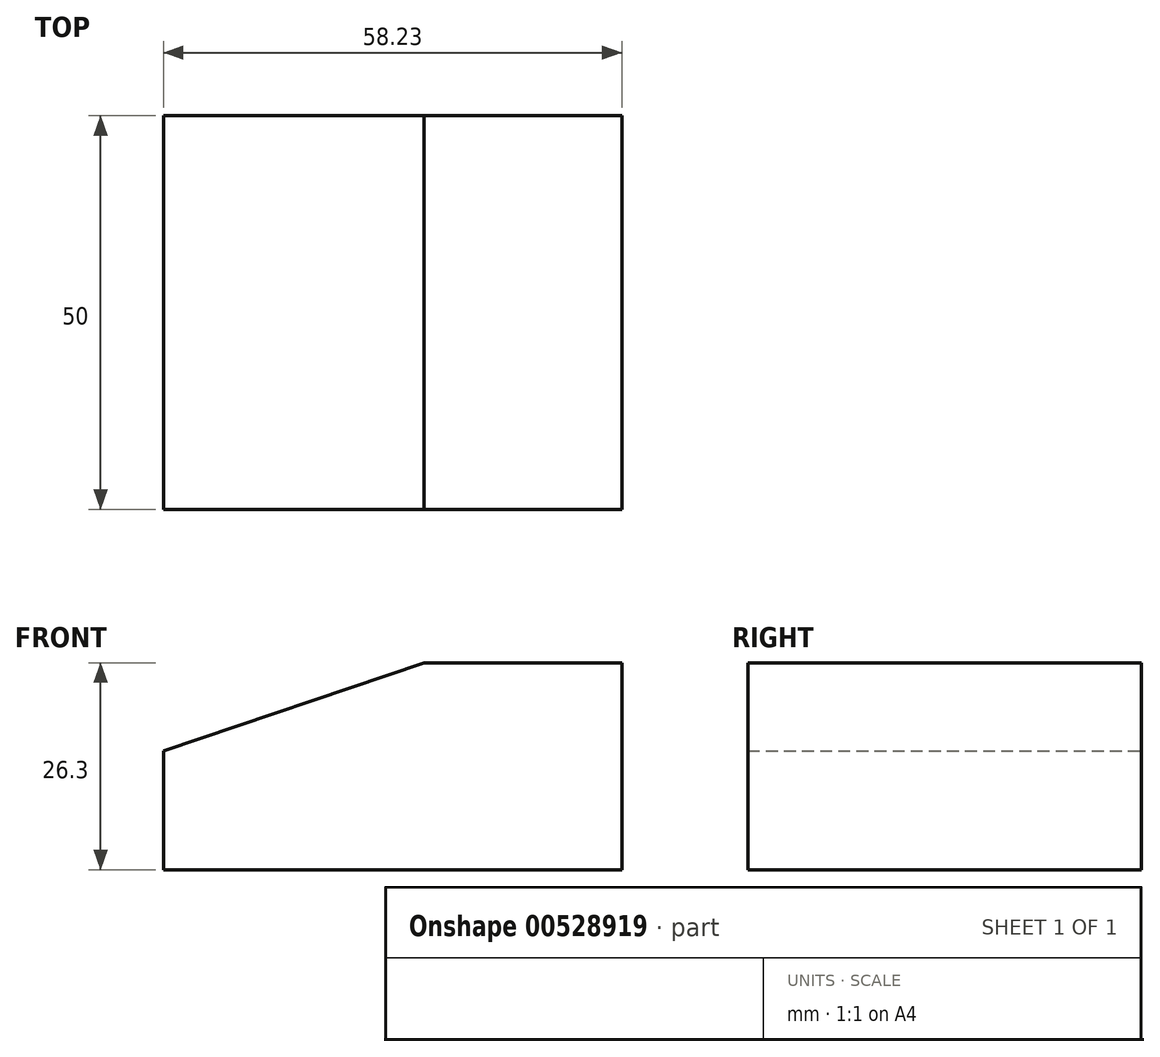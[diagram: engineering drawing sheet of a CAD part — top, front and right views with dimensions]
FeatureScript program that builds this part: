
annotation { "Feature Type Name" : "Feature", "Feature Type Description" : "" }
export const myFeature = defineFeature(function(context is Context, id is Id, definition is map)
    precondition{}
    {
        {
            var Q0;
            Q0=qCreatedBy(makeId("Front.planeOp"),FACE);
            var sketch = newSketch(context, id + "F0", { "sketchPlane" : qUnion([Q0])});
            skLineSegment(sketch, "E0", {"start": v(-58.23, 0) * mm, "end": v(0, 0) * mm});
            skLineSegment(sketch, "E1", {"start": v(0, 0) * mm, "end": v(0, 26.3) * mm});
            skLineSegment(sketch, "E2", {"start": v(0, 26.3) * mm, "end": v(-25.1, 26.3) * mm});
            skLineSegment(sketch, "E3", {"start": v(-25.1, 26.3) * mm, "end": v(-58.23, 15.07) * mm});
            skLineSegment(sketch, "E4", {"start": v(-58.23, 15.07) * mm, "end": v(-58.23, 0) * mm});
            skSolve(sketch);
        }
        {
            var Q0;
            Q0=makeQuery(id+"F0.imprint","IMPRINT",FACE,{"disambiguationData":[TD([[makeQuery(id+"F0.imprint","IMPRINT",EDGE,{"derivedFrom":sQuery(id+"F0.wireOp",EDGE,"E0")}),1.0]])]});
            extrude(context, id + "F1", {"entities" : qUnion([Q0]), "depth" : 25 * mm, "offsetDistance" : 25 * mm, "hasSecondDirection" : true, "secondDirectionOppositeDirection" : true, "secondDirectionDepth" : 25 * mm});
        }
    });
